# Revit family: 1VHS-UN_Straight_DN15-20_RFA
name_source: partatom
category: Pipe Accessories
units: mm (PartAtom-declared; Revit-internal decimal feet)

## family parameters
Always vertical = Yes
Cut with Voids When Loaded = No
OmniClass Number = 23.65.55.14.17
OmniClass Title = Adjusting/Controlling Valves for Liquid Services
Part Type = Valve - Breaks Into
Round Connector Dimension = Use Diameter
Shared = No
Work Plane-Based = No

## types (2) — shared parameters
Application = 2-pipe system
CGAP = 50 mm  [stored 0.164042 ft]
D = 20 mm  [stored 0.0656168 ft]
Description = Thermostatic H-piece Valve
H0 = 28 mm  [stored 0.0918635 ft]
H1 = 3 mm  [stored 0.00984252 ft]
H3 = 17 mm
H4 = 8 mm  [stored 0.0262467 ft]
HH = 46 mm  [stored 0.150919 ft]
IfcExportAs = IfcValveType
IfcExportType = VHS-UN
Kvs = 0.6 m³/h
L1 = 3.3 mm  [stored 0.0108268 ft]
L2 = 80 mm
L2_1 = 40 mm
L2_2 = 36.5 mm  [stored 0.119751 ft]
L3 = 23.1 mm  [stored 0.0757874 ft]
L4 = 12 mm  [stored 0.0393701 ft]
LM = 25 mm  [stored 0.082021 ft]
LOD 200 = No
LOD 350 = Yes
L_1 = 1.8 mm  [stored 0.00590551 ft]
L_2 = 2.5 mm  [stored 0.0082021 ft]
L_3 = 3.4 mm
L_4 = 3.9 mm  [stored 0.0127953 ft]
L_5 = -1.2 mm  [stored -0.00393701 ft]
L_6 = 10.1 mm
L_EQ = 25 mm  [stored 0.082021 ft]
Manufacturer = Danfoss
Max Differential Pressure = 0.6 bar
Max Medium Temperature = 120 °C
Max Operating Pressure = 10 bar
RB1 = 11.7 mm  [stored 0.0383858 ft]
RB2 = 10.3 mm
RN = 13.2 mm
RN1 = 17.4 mm  [stored 0.0570866 ft]
RN2 = 6 mm  [stored 0.019685 ft]
RV1 = 12.5 mm  [stored 0.0410105 ft]
RV2 = 10.5 mm  [stored 0.0344488 ft]
RV3 = 12.8 mm
RV4 = 11.4 mm
RV5 = 8.2 mm  [stored 0.0269029 ft]
RV6 = 10 mm  [stored 0.0328084 ft]
RV7 = 9.5 mm  [stored 0.031168 ft]
RV8 = 1 mm  [stored 0.00328084 ft]
R_nut200 = 17.4 mm  [stored 0.0570866 ft]
TD = 34.8 mm
TH = 74 mm  [stored 0.242782 ft]
TL1 = 67.8 mm
TL2 = 62 mm
URL = https://store.danfoss.com
Valve Body Material = Danfoss Nickel Plated Brass
W_nut1 = 15 mm  [stored 0.0492126 ft]
W_nut2 = 5.2 mm

## per-type parameters (varying)
| type | DR | Model | Model Type | Weight |
| VHS-UN_Straight_DN15-20_013G4742 | 15 mm | 013G4742 | VHS-UN_Straight_DN15-20 | 0.75 kg |
| VHS-UN_Straight_DN20-20_013G4744 | 20 mm | 013G4744 | VHS-UN_Straight_DN20-20 | 0.68 kg |

note: [stored X ft] marks values corroborated as IEEE doubles in the binary element streams (Revit-internal decimal feet)

## geometry (parser evidence)
native form markers: Sweep x4
no freeform markers — native parametric forms only
